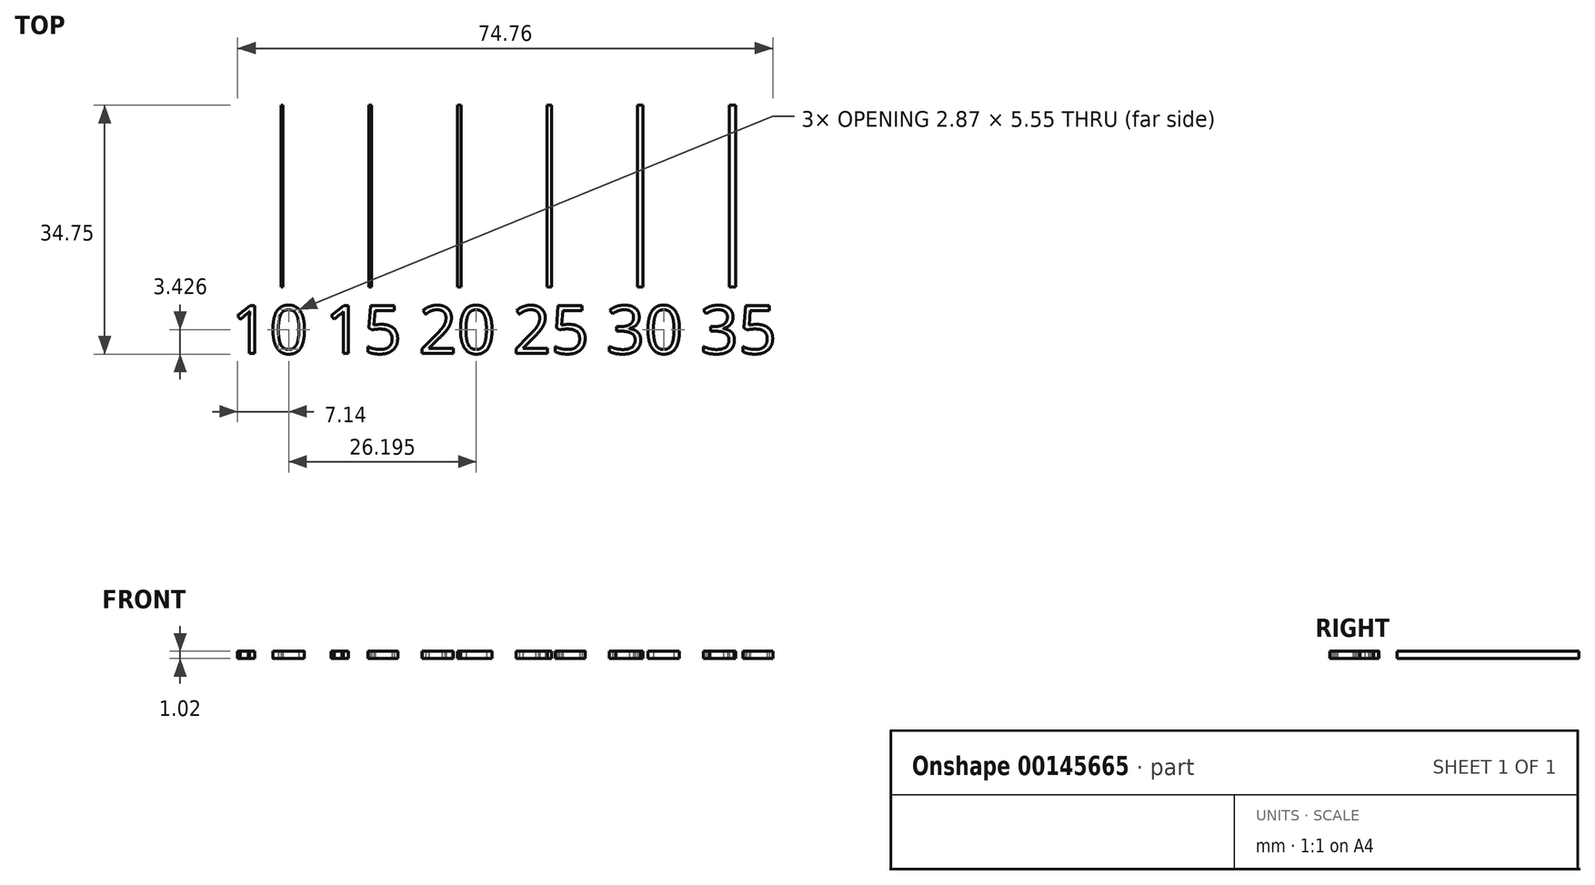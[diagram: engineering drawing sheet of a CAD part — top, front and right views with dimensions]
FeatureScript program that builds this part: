
annotation { "Feature Type Name" : "Feature", "Feature Type Description" : "" }
export const myFeature = defineFeature(function(context is Context, id is Id, definition is map)
    precondition{}
    {
        {
            var Q0;
            Q0=qCreatedBy(makeId("Top.planeOp"),FACE);
            var sketch = newSketch(context, id + "F0", { "sketchPlane" : qUnion([Q0])});
            skLineSegment(sketch, "E0.bottom", {"start": v(-31.18, 0) * mm, "end": v(-30.92, 0) * mm});
            skLineSegment(sketch, "E0.top", {"start": v(-31.18, 25.4) * mm, "end": v(-30.92, 25.4) * mm});
            skLineSegment(sketch, "E0.left", {"start": v(-31.18, 0) * mm, "end": v(-31.18, 25.4) * mm});
            skLineSegment(sketch, "E0.right", {"start": v(-30.92, 0) * mm, "end": v(-30.92, 25.4) * mm});
            skLineSegment(sketch, "E1.bottom", {"start": v(-18.91, 0) * mm, "end": v(-18.53, 0) * mm});
            skLineSegment(sketch, "E1.top", {"start": v(-18.91, 25.4) * mm, "end": v(-18.53, 25.4) * mm});
            skLineSegment(sketch, "E1.left", {"start": v(-18.91, 0) * mm, "end": v(-18.91, 25.4) * mm});
            skLineSegment(sketch, "E1.right", {"start": v(-18.53, 0) * mm, "end": v(-18.53, 25.4) * mm});
            skLineSegment(sketch, "E2.bottom", {"start": v(-6.52, 0) * mm, "end": v(-6, 0) * mm});
            skLineSegment(sketch, "E2.top", {"start": v(-6.52, 25.4) * mm, "end": v(-6, 25.4) * mm});
            skLineSegment(sketch, "E2.left", {"start": v(-6.52, 0) * mm, "end": v(-6.52, 25.4) * mm});
            skLineSegment(sketch, "E2.right", {"start": v(-6, 0) * mm, "end": v(-6, 25.4) * mm});
            skLineSegment(sketch, "E3.bottom", {"start": v(6, 0) * mm, "end": v(6.64, 0) * mm});
            skLineSegment(sketch, "E3.top", {"start": v(6, 25.4) * mm, "end": v(6.64, 25.4) * mm});
            skLineSegment(sketch, "E3.left", {"start": v(6, 0) * mm, "end": v(6, 25.4) * mm});
            skLineSegment(sketch, "E3.right", {"start": v(6.64, 0) * mm, "end": v(6.64, 25.4) * mm});
            skLineSegment(sketch, "E4.bottom", {"start": v(18.66, 0) * mm, "end": v(19.42, 0) * mm});
            skLineSegment(sketch, "E4.top", {"start": v(18.66, 25.4) * mm, "end": v(19.42, 25.4) * mm});
            skLineSegment(sketch, "E4.left", {"start": v(18.66, 0) * mm, "end": v(18.66, 25.4) * mm});
            skLineSegment(sketch, "E4.right", {"start": v(19.42, 0) * mm, "end": v(19.42, 25.4) * mm});
            skLineSegment(sketch, "E5.bottom", {"start": v(31.43, 0) * mm, "end": v(32.32, 0) * mm});
            skLineSegment(sketch, "E5.top", {"start": v(31.43, 25.4) * mm, "end": v(32.32, 25.4) * mm});
            skLineSegment(sketch, "E5.left", {"start": v(31.43, 0) * mm, "end": v(31.43, 25.4) * mm});
            skLineSegment(sketch, "E5.right", {"start": v(32.32, 0) * mm, "end": v(32.32, 25.4) * mm});
            skLineSegment(sketch, "E6", {"start": v(0, 0) * mm, "end": v(0, 25.4) * mm, "construction": true});
            skLineSegment(sketch, "E7", {"start": v(-30.92, 0) * mm, "end": v(-18.91, 0) * mm, "construction": true});
            skLineSegment(sketch, "E8", {"start": v(-18.53, 0) * mm, "end": v(-6.52, 0) * mm, "construction": true});
            skLineSegment(sketch, "E9", {"start": v(-6, 0) * mm, "end": v(6, 0) * mm, "construction": true});
            skLineSegment(sketch, "E10", {"start": v(6.64, 0) * mm, "end": v(18.66, 0) * mm, "construction": true});
            skLineSegment(sketch, "E11", {"start": v(19.42, 0) * mm, "end": v(31.43, 0) * mm, "construction": true});
            skText(sketch, "E12", { "text": "10 15 20 25 30 35\n", "fontName": "OpenSans-Regular.ttf"});
            const initialGuessF0  = {"E12": [-0.0381, -0.00926, 1, 0, 0.00672]};
            skSetInitialGuess(sketch, initialGuessF0);
            skSolve(sketch);
        }
        {
            var Q0;
            Q0 = qSketchRegion(id + "F0", true);
            extrude(context, id + "F1", {"entities" : qUnion([Q0]), "depth" : 1.02 * mm});
        }
    });
